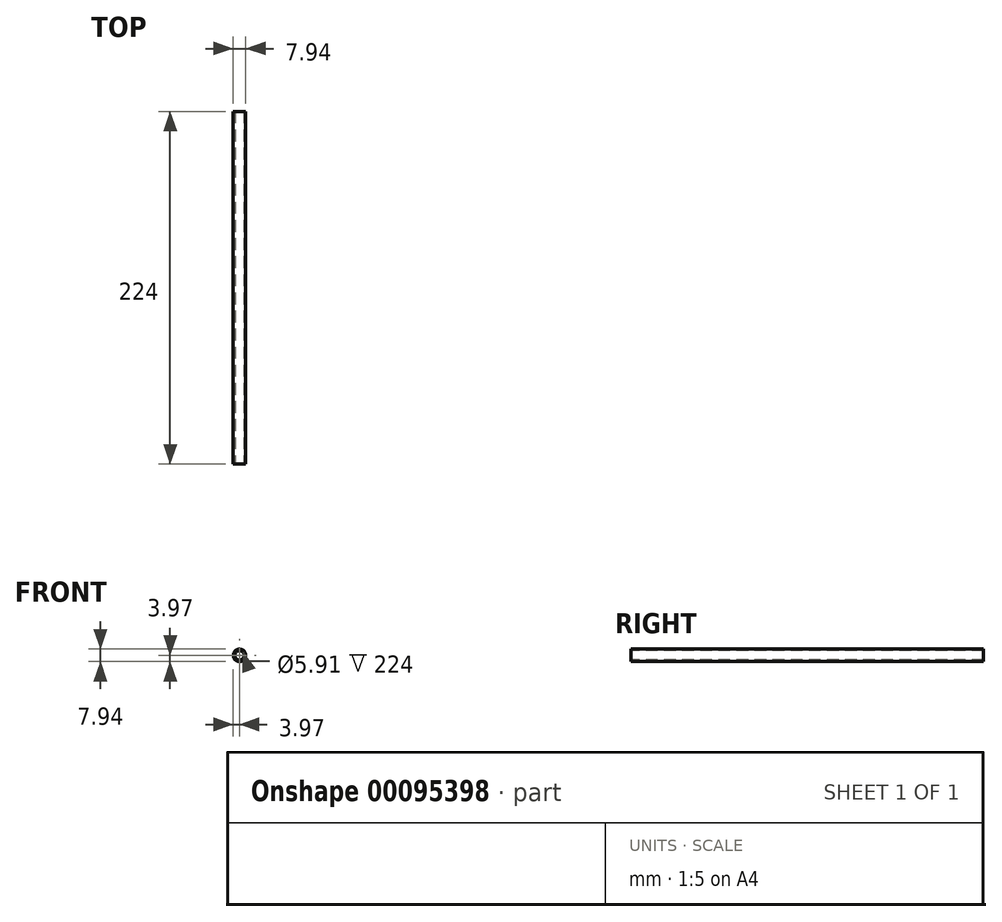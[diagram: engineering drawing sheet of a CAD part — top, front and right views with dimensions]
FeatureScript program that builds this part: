
annotation { "Feature Type Name" : "Feature", "Feature Type Description" : "" }
export const myFeature = defineFeature(function(context is Context, id is Id, definition is map)
    precondition{}
    {
        {
            var Q0;
            Q0=qCreatedBy(makeId("Top.planeOp"),FACE);
            var sketch = newSketch(context, id + "F0", { "sketchPlane" : qUnion([Q0])});
            skLineSegment(sketch, "E0.bottom", {"start": v(2.95, 0) * mm, "end": v(3.97, 0) * mm});
            skLineSegment(sketch, "E0.top", {"start": v(2.95, 224) * mm, "end": v(3.97, 224) * mm});
            skLineSegment(sketch, "E0.left", {"start": v(2.95, 0) * mm, "end": v(2.95, 224) * mm});
            skLineSegment(sketch, "E0.right", {"start": v(3.97, 0) * mm, "end": v(3.97, 224) * mm});
            skLineSegment(sketch, "E1", {"start": v(0, 0) * mm, "end": v(0, 224) * mm, "construction": true});
            skSolve(sketch);
        }
        {
            var Q0;
            Q0 = qSketchRegion(id + "F0", true);
            var Q1;
            Q1=sQuery(id+"F0.wireOp",EDGE,"E1");
            revolve(context, id + "F1", {"entities" : qUnion([Q0]), "axis" : qUnion([Q1]), "revolveType" : RevolveType.FULL});
        }
    });
